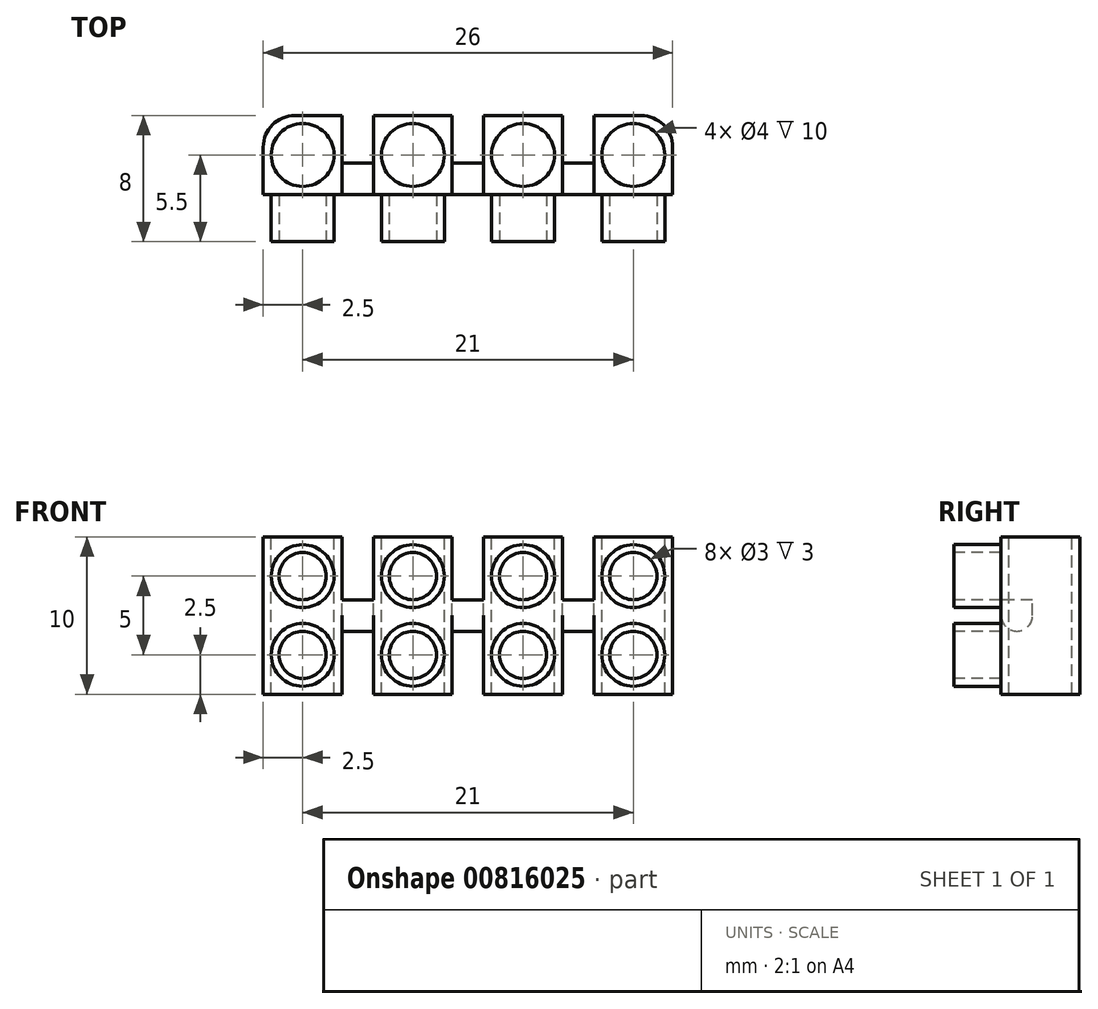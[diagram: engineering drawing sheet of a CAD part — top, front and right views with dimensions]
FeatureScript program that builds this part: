
annotation { "Feature Type Name" : "Feature", "Feature Type Description" : "" }
export const myFeature = defineFeature(function(context is Context, id is Id, definition is map)
    precondition{}
    {
        {
            var Q0;
            Q0=qCreatedBy(makeId("Front.planeOp"),FACE);
            var sketch = newSketch(context, id + "F0", { "sketchPlane" : qUnion([Q0])});
            skLineSegment(sketch, "E0.bottom", {"start": v(-13, 5) * mm, "end": v(13, 5) * mm});
            skLineSegment(sketch, "E0.top", {"start": v(-13, -5) * mm, "end": v(13, -5) * mm});
            skLineSegment(sketch, "E0.left", {"start": v(-13, 5) * mm, "end": v(-13, -5) * mm});
            skLineSegment(sketch, "E0.right", {"start": v(13, 5) * mm, "end": v(13, -5) * mm});
            skPoint(sketch, "E0.middle", {"position": v(0, 0) * mm});
            skSolve(sketch);
        }
        {
            var Q0;
            Q0=makeQuery(id+"F0.imprint","IMPRINT",FACE,{"disambiguationData":[TD([[makeQuery(id+"F0.imprint","IMPRINT",EDGE,{"derivedFrom":sQuery(id+"F0.wireOp",EDGE,"E0.bottom")}),-1.0]])]});
            extrude(context, id + "F1", {"entities" : qUnion([Q0]), "depth" : 8 * mm, "offsetDistance" : 25 * mm, "symmetric" : true});
        }
        {
            var Q0;
            Q0=makeQuery(id+"F1.opExtrude","CAP_FACE",FACE,{"disambiguationData":[OSD([sQuery(id+"F0.wireOp",EDGE,"E0.bottom"),sQuery(id+"F0.wireOp",EDGE,"E0.top"),sQuery(id+"F0.wireOp",EDGE,"E0.left"),sQuery(id+"F0.wireOp",EDGE,"E0.right")])],"isStart":false});
            var sketch = newSketch(context, id + "F2", { "sketchPlane" : qUnion([Q0])});
            skLineSegment(sketch, "E1", {"start": v(-13, 5) * mm, "end": v(-8, 5) * mm});
            skLineSegment(sketch, "E2", {"start": v(-8, 5) * mm, "end": v(-8, 1) * mm});
            skLineSegment(sketch, "E3", {"start": v(-8, 1) * mm, "end": v(-6, 1) * mm});
            skLineSegment(sketch, "E4", {"start": v(-6, 1) * mm, "end": v(-6, 5) * mm});
            skLineSegment(sketch, "E5", {"start": v(-6, 5) * mm, "end": v(-1, 5) * mm});
            skLineSegment(sketch, "E6", {"start": v(-1, 5) * mm, "end": v(-1, 1) * mm});
            skLineSegment(sketch, "E7", {"start": v(-1, 1) * mm, "end": v(1, 1) * mm});
            skLineSegment(sketch, "E8", {"start": v(1, 1) * mm, "end": v(1, 5) * mm});
            skLineSegment(sketch, "E9", {"start": v(1, 5) * mm, "end": v(6, 5) * mm});
            skLineSegment(sketch, "E10", {"start": v(6, 5) * mm, "end": v(6, 1) * mm});
            skLineSegment(sketch, "E11", {"start": v(6, 1) * mm, "end": v(8, 1) * mm});
            skLineSegment(sketch, "E12", {"start": v(8, 1) * mm, "end": v(8, 5) * mm});
            skLineSegment(sketch, "E13", {"start": v(8, 5) * mm, "end": v(13, 5) * mm});
            skLineSegment(sketch, "E14", {"start": v(13, 5) * mm, "end": v(13, -5) * mm});
            skLineSegment(sketch, "E15", {"start": v(13, -5) * mm, "end": v(8, -5) * mm});
            skLineSegment(sketch, "E16", {"start": v(8, -5) * mm, "end": v(8, -1) * mm});
            skLineSegment(sketch, "E17", {"start": v(8, -1) * mm, "end": v(6, -1) * mm});
            skLineSegment(sketch, "E18", {"start": v(6, -1) * mm, "end": v(6, -5) * mm});
            skLineSegment(sketch, "E19", {"start": v(6, -5) * mm, "end": v(1, -5) * mm});
            skLineSegment(sketch, "E20", {"start": v(1, -5) * mm, "end": v(1, -1) * mm});
            skLineSegment(sketch, "E21", {"start": v(1, -1) * mm, "end": v(-1, -1) * mm});
            skLineSegment(sketch, "E22", {"start": v(-1, -1) * mm, "end": v(-1, -5) * mm});
            skLineSegment(sketch, "E23", {"start": v(-1, -5) * mm, "end": v(-6, -5) * mm});
            skLineSegment(sketch, "E24", {"start": v(-6, -5) * mm, "end": v(-6, -1) * mm});
            skLineSegment(sketch, "E25", {"start": v(-6, -1) * mm, "end": v(-8, -1) * mm});
            skLineSegment(sketch, "E26", {"start": v(-8, -1) * mm, "end": v(-8, -5) * mm});
            skLineSegment(sketch, "E27", {"start": v(-8, -5) * mm, "end": v(-13, -5) * mm});
            skLineSegment(sketch, "E28", {"start": v(-13, -5) * mm, "end": v(-13, 5) * mm});
            skSolve(sketch);
        }
        {
            var Q0;
            {var subQ0=sQuery(id+"F2.wireOp",EDGE,"E2");Q0=makeQuery(id+"F2.imprint","IMPRINT",FACE,{"disambiguationData":[TD([[makeQuery(id+"F2.imprint","IMPRINT",EDGE,{"derivedFrom":subQ0}),1.0]])]});}
            var Q1;
            {var subQ0=sQuery(id+"F2.wireOp",EDGE,"E6");Q1=makeQuery(id+"F2.imprint","IMPRINT",FACE,{"disambiguationData":[TD([[makeQuery(id+"F2.imprint","IMPRINT",EDGE,{"derivedFrom":subQ0}),1.0]])]});}
            var Q2;
            {var subQ0=sQuery(id+"F2.wireOp",EDGE,"E10");Q2=makeQuery(id+"F2.imprint","IMPRINT",FACE,{"disambiguationData":[TD([[makeQuery(id+"F2.imprint","IMPRINT",EDGE,{"derivedFrom":subQ0}),1.0]])]});}
            var Q3;
            {var subQ0=sQuery(id+"F2.wireOp",EDGE,"E16");Q3=makeQuery(id+"F2.imprint","IMPRINT",FACE,{"disambiguationData":[TD([[makeQuery(id+"F2.imprint","IMPRINT",EDGE,{"derivedFrom":subQ0}),1.0]])]});}
            var Q4;
            {var subQ0=sQuery(id+"F2.wireOp",EDGE,"E20");Q4=makeQuery(id+"F2.imprint","IMPRINT",FACE,{"disambiguationData":[TD([[makeQuery(id+"F2.imprint","IMPRINT",EDGE,{"derivedFrom":subQ0}),1.0]])]});}
            var Q5;
            {var subQ0=sQuery(id+"F2.wireOp",EDGE,"E24");Q5=makeQuery(id+"F2.imprint","IMPRINT",FACE,{"disambiguationData":[TD([[makeQuery(id+"F2.imprint","IMPRINT",EDGE,{"derivedFrom":subQ0}),1.0]])]});}
            extrude(context, id + "F3", {"entities" : qUnion([Q0, Q1, Q2, Q3, Q4, Q5]), "operationType" : NewBodyOperationType.REMOVE, "oppositeDirection" : true, "depth" : 25 * mm, "offsetDistance" : 25 * mm});
        }
        {
            var Q0;
            Q0=makeQuery(id+"F3.boolean.opBoolean","COPY",FACE,{"derivedFrom":makeQuery(id+"F3.opExtrude","SWEPT_FACE",FACE,{"disambiguationData":[OSD([sQuery(id+"F2.wireOp",EDGE,"E7")])]})});
            var sketch = newSketch(context, id + "F4", { "sketchPlane" : qUnion([Q0])});
            skLineSegment(sketch, "E29.bottom", {"start": v(-1, -4) * mm, "end": v(1, -4) * mm});
            skLineSegment(sketch, "E29.top", {"start": v(-1, -1) * mm, "end": v(1, -1) * mm});
            skLineSegment(sketch, "E29.left", {"start": v(-1, -4) * mm, "end": v(-1, -1) * mm});
            skLineSegment(sketch, "E29.right", {"start": v(1, -4) * mm, "end": v(1, -1) * mm});
            skLineSegment(sketch, "E30.bottom", {"start": v(-1, 4) * mm, "end": v(1, 4) * mm});
            skLineSegment(sketch, "E30.top", {"start": v(-1, 1) * mm, "end": v(1, 1) * mm});
            skLineSegment(sketch, "E30.left", {"start": v(-1, 4) * mm, "end": v(-1, 1) * mm});
            skLineSegment(sketch, "E30.right", {"start": v(1, 4) * mm, "end": v(1, 1) * mm});
            skSolve(sketch);
        }
        {
            var Q0;
            Q0=makeQuery(id+"F3.boolean.opBoolean","COPY",FACE,{"derivedFrom":makeQuery(id+"F3.opExtrude","SWEPT_FACE",FACE,{"disambiguationData":[OSD([sQuery(id+"F2.wireOp",EDGE,"E11")])]})});
            var sketch = newSketch(context, id + "F5", { "sketchPlane" : qUnion([Q0])});
            skLineSegment(sketch, "E31.bottom", {"start": v(8, 4) * mm, "end": v(6, 4) * mm});
            skLineSegment(sketch, "E31.top", {"start": v(8, 1) * mm, "end": v(6, 1) * mm});
            skLineSegment(sketch, "E31.left", {"start": v(8, 4) * mm, "end": v(8, 1) * mm});
            skLineSegment(sketch, "E31.right", {"start": v(6, 4) * mm, "end": v(6, 1) * mm});
            skLineSegment(sketch, "E32.bottom", {"start": v(8, -4) * mm, "end": v(6, -4) * mm});
            skLineSegment(sketch, "E32.top", {"start": v(8, -1) * mm, "end": v(6, -1) * mm});
            skLineSegment(sketch, "E32.left", {"start": v(8, -4) * mm, "end": v(8, -1) * mm});
            skLineSegment(sketch, "E32.right", {"start": v(6, -4) * mm, "end": v(6, -1) * mm});
            skSolve(sketch);
        }
        {
            var Q0;
            Q0=makeQuery(id+"F3.boolean.opBoolean","COPY",FACE,{"derivedFrom":makeQuery(id+"F3.opExtrude","SWEPT_FACE",FACE,{"disambiguationData":[OSD([sQuery(id+"F2.wireOp",EDGE,"E3")])]})});
            var sketch = newSketch(context, id + "F6", { "sketchPlane" : qUnion([Q0])});
            skLineSegment(sketch, "E33.bottom", {"start": v(-6, -4) * mm, "end": v(-8, -4) * mm});
            skLineSegment(sketch, "E33.top", {"start": v(-6, -1) * mm, "end": v(-8, -1) * mm});
            skLineSegment(sketch, "E33.left", {"start": v(-6, -4) * mm, "end": v(-6, -1) * mm});
            skLineSegment(sketch, "E33.right", {"start": v(-8, -4) * mm, "end": v(-8, -1) * mm});
            skLineSegment(sketch, "E34.bottom", {"start": v(-6, 4) * mm, "end": v(-8, 4) * mm});
            skLineSegment(sketch, "E34.top", {"start": v(-6, 1) * mm, "end": v(-8, 1) * mm});
            skLineSegment(sketch, "E34.left", {"start": v(-6, 4) * mm, "end": v(-6, 1) * mm});
            skLineSegment(sketch, "E34.right", {"start": v(-8, 4) * mm, "end": v(-8, 1) * mm});
            skSolve(sketch);
        }
        {
            var Q0;
            Q0=makeQuery(id+"F4.imprint","IMPRINT",FACE,{"disambiguationData":[TD([[makeQuery(id+"F4.imprint","IMPRINT",EDGE,{"derivedFrom":sQuery(id+"F4.wireOp",EDGE,"E30.bottom")}),-1.0]])]});
            var Q1;
            Q1=makeQuery(id+"F4.imprint","IMPRINT",FACE,{"disambiguationData":[TD([[makeQuery(id+"F4.imprint","IMPRINT",EDGE,{"derivedFrom":sQuery(id+"F4.wireOp",EDGE,"E29.bottom")}),1.0]])]});
            var Q2;
            Q2=makeQuery(id+"F5.imprint","IMPRINT",FACE,{"disambiguationData":[TD([[makeQuery(id+"F5.imprint","IMPRINT",EDGE,{"derivedFrom":sQuery(id+"F5.wireOp",EDGE,"E31.bottom")}),-1.0]])]});
            var Q3;
            Q3=makeQuery(id+"F5.imprint","IMPRINT",FACE,{"disambiguationData":[TD([[makeQuery(id+"F5.imprint","IMPRINT",EDGE,{"derivedFrom":sQuery(id+"F5.wireOp",EDGE,"E32.bottom")}),1.0]])]});
            var Q4;
            Q4=makeQuery(id+"F6.imprint","IMPRINT",FACE,{"disambiguationData":[TD([[makeQuery(id+"F6.imprint","IMPRINT",EDGE,{"derivedFrom":sQuery(id+"F6.wireOp",EDGE,"E33.bottom")}),1.0]])]});
            var Q5;
            Q5=makeQuery(id+"F6.imprint","IMPRINT",FACE,{"disambiguationData":[TD([[makeQuery(id+"F6.imprint","IMPRINT",EDGE,{"derivedFrom":sQuery(id+"F6.wireOp",EDGE,"E34.bottom")}),-1.0]])]});
            extrude(context, id + "F7", {"entities" : qUnion([Q0, Q1, Q2, Q3, Q4, Q5]), "operationType" : NewBodyOperationType.REMOVE, "oppositeDirection" : true, "depth" : 25 * mm, "offsetDistance" : 25 * mm});
        }
        {
            var Q0;
            Q0=makeQuery(id+"F1.opExtrude","CAP_EDGE",EDGE,{"disambiguationData":[OSD([sQuery(id+"F0.wireOp",EDGE,"E0.left")])],"isStart":true});
            var Q1;
            {var subQ0=makeQuery(id+"F1.opExtrude","CAP_FACE",FACE,{"disambiguationData":[OSD([sQuery(id+"F0.wireOp",EDGE,"E0.bottom"),sQuery(id+"F0.wireOp",EDGE,"E0.top"),sQuery(id+"F0.wireOp",EDGE,"E0.left"),sQuery(id+"F0.wireOp",EDGE,"E0.right")])],"isStart":true});Q1=makeQuery(id+"F7.boolean.opBoolean","MERGE",EDGE,{"derivedFrom":[makeQuery(id+"F3.boolean.opBoolean","INTERSECT",EDGE,{"derivedFrom":[subQ0,makeQuery(id+"F3.opExtrude","SWEPT_FACE",FACE,{"disambiguationData":[OSD([sQuery(id+"F2.wireOp",EDGE,"E2")])]})]}),makeQuery(id+"F3.boolean.opBoolean","INTERSECT",EDGE,{"derivedFrom":[subQ0,makeQuery(id+"F3.opExtrude","SWEPT_FACE",FACE,{"disambiguationData":[OSD([sQuery(id+"F2.wireOp",EDGE,"E26")])]})]}),makeQuery(id+"F7.opExtrude","SWEPT_EDGE",EDGE,{"disambiguationData":[OSD([sQuery(id+"F6.wireOp",EDGE,"E34.bottom"),sQuery(id+"F6.wireOp",EDGE,"E34.right")])]})]});}
            var Q2;
            {var subQ0=makeQuery(id+"F1.opExtrude","CAP_FACE",FACE,{"disambiguationData":[OSD([sQuery(id+"F0.wireOp",EDGE,"E0.bottom"),sQuery(id+"F0.wireOp",EDGE,"E0.top"),sQuery(id+"F0.wireOp",EDGE,"E0.left"),sQuery(id+"F0.wireOp",EDGE,"E0.right")])],"isStart":true});Q2=makeQuery(id+"F7.boolean.opBoolean","MERGE",EDGE,{"derivedFrom":[makeQuery(id+"F3.boolean.opBoolean","INTERSECT",EDGE,{"derivedFrom":[subQ0,makeQuery(id+"F3.opExtrude","SWEPT_FACE",FACE,{"disambiguationData":[OSD([sQuery(id+"F2.wireOp",EDGE,"E4")])]})]}),makeQuery(id+"F3.boolean.opBoolean","INTERSECT",EDGE,{"derivedFrom":[subQ0,makeQuery(id+"F3.opExtrude","SWEPT_FACE",FACE,{"disambiguationData":[OSD([sQuery(id+"F2.wireOp",EDGE,"E24")])]})]}),makeQuery(id+"F7.opExtrude","SWEPT_EDGE",EDGE,{"disambiguationData":[OSD([sQuery(id+"F6.wireOp",EDGE,"E34.bottom"),sQuery(id+"F6.wireOp",EDGE,"E34.left")])]})]});}
            var Q3;
            {var subQ0=makeQuery(id+"F1.opExtrude","CAP_FACE",FACE,{"disambiguationData":[OSD([sQuery(id+"F0.wireOp",EDGE,"E0.bottom"),sQuery(id+"F0.wireOp",EDGE,"E0.top"),sQuery(id+"F0.wireOp",EDGE,"E0.left"),sQuery(id+"F0.wireOp",EDGE,"E0.right")])],"isStart":true});Q3=makeQuery(id+"F7.boolean.opBoolean","MERGE",EDGE,{"derivedFrom":[makeQuery(id+"F3.boolean.opBoolean","INTERSECT",EDGE,{"derivedFrom":[subQ0,makeQuery(id+"F3.opExtrude","SWEPT_FACE",FACE,{"disambiguationData":[OSD([sQuery(id+"F2.wireOp",EDGE,"E6")])]})]}),makeQuery(id+"F3.boolean.opBoolean","INTERSECT",EDGE,{"derivedFrom":[subQ0,makeQuery(id+"F3.opExtrude","SWEPT_FACE",FACE,{"disambiguationData":[OSD([sQuery(id+"F2.wireOp",EDGE,"E22")])]})]}),makeQuery(id+"F7.opExtrude","SWEPT_EDGE",EDGE,{"disambiguationData":[OSD([sQuery(id+"F4.wireOp",EDGE,"E30.bottom"),sQuery(id+"F4.wireOp",EDGE,"E30.left")])]})]});}
            var Q4;
            {var subQ0=makeQuery(id+"F1.opExtrude","CAP_FACE",FACE,{"disambiguationData":[OSD([sQuery(id+"F0.wireOp",EDGE,"E0.bottom"),sQuery(id+"F0.wireOp",EDGE,"E0.top"),sQuery(id+"F0.wireOp",EDGE,"E0.left"),sQuery(id+"F0.wireOp",EDGE,"E0.right")])],"isStart":true});Q4=makeQuery(id+"F7.boolean.opBoolean","MERGE",EDGE,{"derivedFrom":[makeQuery(id+"F3.boolean.opBoolean","INTERSECT",EDGE,{"derivedFrom":[subQ0,makeQuery(id+"F3.opExtrude","SWEPT_FACE",FACE,{"disambiguationData":[OSD([sQuery(id+"F2.wireOp",EDGE,"E8")])]})]}),makeQuery(id+"F3.boolean.opBoolean","INTERSECT",EDGE,{"derivedFrom":[subQ0,makeQuery(id+"F3.opExtrude","SWEPT_FACE",FACE,{"disambiguationData":[OSD([sQuery(id+"F2.wireOp",EDGE,"E20")])]})]}),makeQuery(id+"F7.opExtrude","SWEPT_EDGE",EDGE,{"disambiguationData":[OSD([sQuery(id+"F4.wireOp",EDGE,"E30.bottom"),sQuery(id+"F4.wireOp",EDGE,"E30.right")])]})]});}
            var Q5;
            {var subQ0=makeQuery(id+"F1.opExtrude","CAP_FACE",FACE,{"disambiguationData":[OSD([sQuery(id+"F0.wireOp",EDGE,"E0.bottom"),sQuery(id+"F0.wireOp",EDGE,"E0.top"),sQuery(id+"F0.wireOp",EDGE,"E0.left"),sQuery(id+"F0.wireOp",EDGE,"E0.right")])],"isStart":true});Q5=makeQuery(id+"F7.boolean.opBoolean","MERGE",EDGE,{"derivedFrom":[makeQuery(id+"F3.boolean.opBoolean","INTERSECT",EDGE,{"derivedFrom":[subQ0,makeQuery(id+"F3.opExtrude","SWEPT_FACE",FACE,{"disambiguationData":[OSD([sQuery(id+"F2.wireOp",EDGE,"E10")])]})]}),makeQuery(id+"F3.boolean.opBoolean","INTERSECT",EDGE,{"derivedFrom":[subQ0,makeQuery(id+"F3.opExtrude","SWEPT_FACE",FACE,{"disambiguationData":[OSD([sQuery(id+"F2.wireOp",EDGE,"E18")])]})]}),makeQuery(id+"F7.opExtrude","SWEPT_EDGE",EDGE,{"disambiguationData":[OSD([sQuery(id+"F5.wireOp",EDGE,"E31.bottom"),sQuery(id+"F5.wireOp",EDGE,"E31.right")])]})]});}
            var Q6;
            {var subQ0=makeQuery(id+"F1.opExtrude","CAP_FACE",FACE,{"disambiguationData":[OSD([sQuery(id+"F0.wireOp",EDGE,"E0.bottom"),sQuery(id+"F0.wireOp",EDGE,"E0.top"),sQuery(id+"F0.wireOp",EDGE,"E0.left"),sQuery(id+"F0.wireOp",EDGE,"E0.right")])],"isStart":true});Q6=makeQuery(id+"F7.boolean.opBoolean","MERGE",EDGE,{"derivedFrom":[makeQuery(id+"F3.boolean.opBoolean","INTERSECT",EDGE,{"derivedFrom":[subQ0,makeQuery(id+"F3.opExtrude","SWEPT_FACE",FACE,{"disambiguationData":[OSD([sQuery(id+"F2.wireOp",EDGE,"E12")])]})]}),makeQuery(id+"F3.boolean.opBoolean","INTERSECT",EDGE,{"derivedFrom":[subQ0,makeQuery(id+"F3.opExtrude","SWEPT_FACE",FACE,{"disambiguationData":[OSD([sQuery(id+"F2.wireOp",EDGE,"E16")])]})]}),makeQuery(id+"F7.opExtrude","SWEPT_EDGE",EDGE,{"disambiguationData":[OSD([sQuery(id+"F5.wireOp",EDGE,"E31.bottom"),sQuery(id+"F5.wireOp",EDGE,"E31.left")])]})]});}
            var Q7;
            Q7=makeQuery(id+"F1.opExtrude","CAP_EDGE",EDGE,{"disambiguationData":[OSD([sQuery(id+"F0.wireOp",EDGE,"E0.right")])],"isStart":true});
            fillet(context, id + "F8", {"entities" : qUnion([Q0, Q1, Q2, Q3, Q4, Q5, Q6, Q7]), "radius" : 2 * mm, "tangentPropagation" : true, "allowEdgeOverflow" : false});
        }
        {
            var Q0;
            {var subQ1=sQuery(id+"F0.wireOp",EDGE,"E0.left");var subQ3=sQuery(id+"F0.wireOp",EDGE,"E0.bottom");Q0=makeQuery(id+"F3.boolean.opBoolean","SPLIT",FACE,{"disambiguationData":[TD([makeQuery(id+"F1.opExtrude","SWEPT_FACE",FACE,{"disambiguationData":[OSD([subQ1])]})])],"derivedFrom":makeQuery(id+"F1.opExtrude","SWEPT_FACE",FACE,{"disambiguationData":[OSD([subQ3])]})});}
            var sketch = newSketch(context, id + "F9", { "sketchPlane" : qUnion([Q0])});
            skLineSegment(sketch, "E35", {"start": v(-10.5, 4) * mm, "end": v(-10.5, 1.5) * mm});
            skCircle(sketch, "E36", {"center": v(-10.5, 1.5) * mm, "radius": 2 * mm});
            skSolve(sketch);
        }
        {
            var Q0;
            {var subQ3=sQuery(id+"F0.wireOp",EDGE,"E0.bottom");Q0=makeQuery(id+"F3.boolean.opBoolean","SPLIT",FACE,{"disambiguationData":[TD([makeQuery(id+"F3.opExtrude","SWEPT_FACE",FACE,{"disambiguationData":[OSD([sQuery(id+"F2.wireOp",EDGE,"E4")])]})])],"derivedFrom":makeQuery(id+"F1.opExtrude","SWEPT_FACE",FACE,{"disambiguationData":[OSD([subQ3])]})});}
            var sketch = newSketch(context, id + "F10", { "sketchPlane" : qUnion([Q0])});
            skLineSegment(sketch, "E37", {"start": v(-3.5, 4) * mm, "end": v(-3.5, 1.5) * mm});
            skCircle(sketch, "E38", {"center": v(-3.5, 1.5) * mm, "radius": 2 * mm});
            skSolve(sketch);
        }
        {
            var Q0;
            {var subQ3=sQuery(id+"F0.wireOp",EDGE,"E0.bottom");Q0=makeQuery(id+"F3.boolean.opBoolean","SPLIT",FACE,{"disambiguationData":[TD([makeQuery(id+"F3.opExtrude","SWEPT_FACE",FACE,{"disambiguationData":[OSD([sQuery(id+"F2.wireOp",EDGE,"E8")])]})])],"derivedFrom":makeQuery(id+"F1.opExtrude","SWEPT_FACE",FACE,{"disambiguationData":[OSD([subQ3])]})});}
            var sketch = newSketch(context, id + "F11", { "sketchPlane" : qUnion([Q0])});
            skLineSegment(sketch, "E39", {"start": v(3.5, 4) * mm, "end": v(3.5, 1.5) * mm});
            skCircle(sketch, "E40", {"center": v(3.5, 1.5) * mm, "radius": 2 * mm});
            skSolve(sketch);
        }
        {
            var Q0;
            {var subQ0=sQuery(id+"F0.wireOp",EDGE,"E0.right");var subQ3=sQuery(id+"F0.wireOp",EDGE,"E0.bottom");Q0=makeQuery(id+"F3.boolean.opBoolean","SPLIT",FACE,{"disambiguationData":[TD([makeQuery(id+"F1.opExtrude","SWEPT_FACE",FACE,{"disambiguationData":[OSD([subQ0])]})])],"derivedFrom":makeQuery(id+"F1.opExtrude","SWEPT_FACE",FACE,{"disambiguationData":[OSD([subQ3])]})});}
            var sketch = newSketch(context, id + "F12", { "sketchPlane" : qUnion([Q0])});
            skLineSegment(sketch, "E41", {"start": v(10.5, 4) * mm, "end": v(10.5, 1.5) * mm});
            skCircle(sketch, "E42", {"center": v(10.5, 1.5) * mm, "radius": 2 * mm});
            skSolve(sketch);
        }
        {
            var Q0;
            Q0=makeQuery(id+"F10.imprint","IMPRINT",FACE,{"disambiguationData":[TD([[makeQuery(id+"F10.imprint","IMPRINT",EDGE,{"derivedFrom":sQuery(id+"F10.wireOp",EDGE,"E38")}),1.0]])]});
            var Q1;
            Q1=makeQuery(id+"F11.imprint","IMPRINT",FACE,{"disambiguationData":[TD([[makeQuery(id+"F11.imprint","IMPRINT",EDGE,{"derivedFrom":sQuery(id+"F11.wireOp",EDGE,"E40")}),1.0]])]});
            var Q2;
            Q2=makeQuery(id+"F12.imprint","IMPRINT",FACE,{"disambiguationData":[TD([[makeQuery(id+"F12.imprint","IMPRINT",EDGE,{"derivedFrom":sQuery(id+"F12.wireOp",EDGE,"E42")}),1.0]])]});
            var Q3;
            {var subQ2=sQuery(id+"F0.wireOp",EDGE,"E0.top");Q3=makeQuery(id+"F3.boolean.opBoolean","SPLIT",FACE,{"disambiguationData":[TD([makeQuery(id+"F3.opExtrude","SWEPT_FACE",FACE,{"disambiguationData":[OSD([sQuery(id+"F2.wireOp",EDGE,"E22")])]})])],"derivedFrom":makeQuery(id+"F1.opExtrude","SWEPT_FACE",FACE,{"disambiguationData":[OSD([subQ2])]})});}
            var Q4;
            Q4=makeQuery(id+"F9.imprint","IMPRINT",FACE,{"disambiguationData":[TD([[makeQuery(id+"F9.imprint","IMPRINT",EDGE,{"derivedFrom":sQuery(id+"F9.wireOp",EDGE,"E36")}),1.0]])]});
            extrude(context, id + "F13", {"entities" : qUnion([Q0, Q1, Q2, Q3, Q4]), "operationType" : NewBodyOperationType.REMOVE, "oppositeDirection" : true, "depth" : 25 * mm, "offsetDistance" : 25 * mm});
        }
        {
            var Q0;
            Q0=makeQuery(id+"F7.boolean.opBoolean","COPY",EDGE,{"derivedFrom":makeQuery(id+"F7.opExtrude","CAP_EDGE",EDGE,{"disambiguationData":[OSD([sQuery(id+"F6.wireOp",EDGE,"E33.top")])],"isStart":true})});
            var Q1;
            Q1=makeQuery(id+"F7.boolean.opBoolean","INTERSECT",EDGE,{"derivedFrom":[makeQuery(id+"F3.boolean.opBoolean","COPY",FACE,{"derivedFrom":makeQuery(id+"F3.opExtrude","SWEPT_FACE",FACE,{"disambiguationData":[OSD([sQuery(id+"F2.wireOp",EDGE,"E25")])]})}),makeQuery(id+"F7.opExtrude","SWEPT_FACE",FACE,{"disambiguationData":[OSD([sQuery(id+"F6.wireOp",EDGE,"E33.top")])]})]});
            var Q2;
            Q2=makeQuery(id+"F7.boolean.opBoolean","COPY",EDGE,{"derivedFrom":makeQuery(id+"F7.opExtrude","CAP_EDGE",EDGE,{"disambiguationData":[OSD([sQuery(id+"F4.wireOp",EDGE,"E29.top")])],"isStart":true})});
            var Q3;
            Q3=makeQuery(id+"F7.boolean.opBoolean","INTERSECT",EDGE,{"derivedFrom":[makeQuery(id+"F3.boolean.opBoolean","COPY",FACE,{"derivedFrom":makeQuery(id+"F3.opExtrude","SWEPT_FACE",FACE,{"disambiguationData":[OSD([sQuery(id+"F2.wireOp",EDGE,"E21")])]})}),makeQuery(id+"F7.opExtrude","SWEPT_FACE",FACE,{"disambiguationData":[OSD([sQuery(id+"F4.wireOp",EDGE,"E29.top")])]})]});
            var Q4;
            Q4=makeQuery(id+"F7.boolean.opBoolean","COPY",EDGE,{"derivedFrom":makeQuery(id+"F7.opExtrude","CAP_EDGE",EDGE,{"disambiguationData":[OSD([sQuery(id+"F5.wireOp",EDGE,"E32.top")])],"isStart":true})});
            var Q5;
            Q5=makeQuery(id+"F7.boolean.opBoolean","INTERSECT",EDGE,{"derivedFrom":[makeQuery(id+"F3.boolean.opBoolean","COPY",FACE,{"derivedFrom":makeQuery(id+"F3.opExtrude","SWEPT_FACE",FACE,{"disambiguationData":[OSD([sQuery(id+"F2.wireOp",EDGE,"E17")])]})}),makeQuery(id+"F7.opExtrude","SWEPT_FACE",FACE,{"disambiguationData":[OSD([sQuery(id+"F5.wireOp",EDGE,"E32.top")])]})]});
            var Q6;
            Q6=makeQuery(id+"F7.boolean.opBoolean","COPY",EDGE,{"derivedFrom":makeQuery(id+"F7.opExtrude","CAP_EDGE",EDGE,{"disambiguationData":[OSD([sQuery(id+"F4.wireOp",EDGE,"E30.top")])],"isStart":true})});
            var Q7;
            Q7=makeQuery(id+"F7.boolean.opBoolean","INTERSECT",EDGE,{"derivedFrom":[makeQuery(id+"F3.boolean.opBoolean","COPY",FACE,{"derivedFrom":makeQuery(id+"F3.opExtrude","SWEPT_FACE",FACE,{"disambiguationData":[OSD([sQuery(id+"F2.wireOp",EDGE,"E21")])]})}),makeQuery(id+"F7.opExtrude","SWEPT_FACE",FACE,{"disambiguationData":[OSD([sQuery(id+"F4.wireOp",EDGE,"E30.top")])]})]});
            var Q8;
            Q8=makeQuery(id+"F7.boolean.opBoolean","INTERSECT",EDGE,{"derivedFrom":[makeQuery(id+"F3.boolean.opBoolean","COPY",FACE,{"derivedFrom":makeQuery(id+"F3.opExtrude","SWEPT_FACE",FACE,{"disambiguationData":[OSD([sQuery(id+"F2.wireOp",EDGE,"E25")])]})}),makeQuery(id+"F7.opExtrude","SWEPT_FACE",FACE,{"disambiguationData":[OSD([sQuery(id+"F6.wireOp",EDGE,"E34.top")])]})]});
            var Q9;
            Q9=makeQuery(id+"F7.boolean.opBoolean","COPY",EDGE,{"derivedFrom":makeQuery(id+"F7.opExtrude","CAP_EDGE",EDGE,{"disambiguationData":[OSD([sQuery(id+"F6.wireOp",EDGE,"E34.top")])],"isStart":true})});
            var Q10;
            Q10=makeQuery(id+"F7.boolean.opBoolean","INTERSECT",EDGE,{"derivedFrom":[makeQuery(id+"F3.boolean.opBoolean","COPY",FACE,{"derivedFrom":makeQuery(id+"F3.opExtrude","SWEPT_FACE",FACE,{"disambiguationData":[OSD([sQuery(id+"F2.wireOp",EDGE,"E17")])]})}),makeQuery(id+"F7.opExtrude","SWEPT_FACE",FACE,{"disambiguationData":[OSD([sQuery(id+"F5.wireOp",EDGE,"E31.top")])]})]});
            var Q11;
            Q11=makeQuery(id+"F7.boolean.opBoolean","COPY",EDGE,{"derivedFrom":makeQuery(id+"F7.opExtrude","CAP_EDGE",EDGE,{"disambiguationData":[OSD([sQuery(id+"F5.wireOp",EDGE,"E31.top")])],"isStart":true})});
            fillet(context, id + "F14", {"entities" : qUnion([Q0, Q1, Q2, Q3, Q4, Q5, Q6, Q7, Q8, Q9, Q10, Q11]), "radius" : 1 * mm, "tangentPropagation" : true, "allowEdgeOverflow" : false});
        }
        {
            var Q0;
            {var subQ0=sQuery(id+"F0.wireOp",EDGE,"E0.left");var subQ1=sQuery(id+"F0.wireOp",EDGE,"E0.top");var subQ2=sQuery(id+"F0.wireOp",EDGE,"E0.bottom");Q0=makeQuery(id+"F7.boolean.opBoolean","SPLIT",FACE,{"disambiguationData":[TD([makeQuery(id+"F1.opExtrude","SWEPT_FACE",FACE,{"disambiguationData":[OSD([subQ0])]})])],"derivedFrom":makeQuery(id+"F1.opExtrude","CAP_FACE",FACE,{"disambiguationData":[OSD([subQ2,subQ1,subQ0,sQuery(id+"F0.wireOp",EDGE,"E0.right")])],"isStart":false})});}
            var sketch = newSketch(context, id + "F15", { "sketchPlane" : qUnion([Q0])});
            skLineSegment(sketch, "E43", {"start": v(-10.5, 5) * mm, "end": v(-10.5, 2.5) * mm});
            skLineSegment(sketch, "E44", {"start": v(-10.5, 2.5) * mm, "end": v(-10.5, -2.5) * mm});
            skCircle(sketch, "E45", {"center": v(-10.5, 2.5) * mm, "radius": 1.5 * mm});
            skCircle(sketch, "E46", {"center": v(-10.5, -2.5) * mm, "radius": 1.5 * mm});
            skCircle(sketch, "E47.0", {"center": v(-10.5, 2.5) * mm, "radius": 2 * mm});
            skCircle(sketch, "E48.0", {"center": v(-10.5, -2.5) * mm, "radius": 2 * mm});
            skSolve(sketch);
        }
        {
            var Q0;
            {var subQ0=sQuery(id+"F0.wireOp",EDGE,"E0.top");var subQ1=sQuery(id+"F0.wireOp",EDGE,"E0.bottom");Q0=makeQuery(id+"F7.boolean.opBoolean","SPLIT",FACE,{"disambiguationData":[TD([makeQuery(id+"F3.boolean.opBoolean","COPY",FACE,{"derivedFrom":makeQuery(id+"F3.opExtrude","SWEPT_FACE",FACE,{"disambiguationData":[OSD([sQuery(id+"F2.wireOp",EDGE,"E4")])]})})])],"derivedFrom":makeQuery(id+"F1.opExtrude","CAP_FACE",FACE,{"disambiguationData":[OSD([subQ1,subQ0,sQuery(id+"F0.wireOp",EDGE,"E0.left"),sQuery(id+"F0.wireOp",EDGE,"E0.right")])],"isStart":false})});}
            var sketch = newSketch(context, id + "F16", { "sketchPlane" : qUnion([Q0])});
            skLineSegment(sketch, "E49", {"start": v(-3.5, 5) * mm, "end": v(-3.5, 2.5) * mm});
            skLineSegment(sketch, "E50", {"start": v(-3.5, 2.5) * mm, "end": v(-3.5, -2.5) * mm});
            skCircle(sketch, "E51", {"center": v(-3.5, 2.5) * mm, "radius": 1.5 * mm});
            skCircle(sketch, "E52", {"center": v(-3.5, -2.5) * mm, "radius": 1.5 * mm});
            skCircle(sketch, "E53.0", {"center": v(-3.5, 2.5) * mm, "radius": 2 * mm});
            skCircle(sketch, "E54.0", {"center": v(-3.5, -2.5) * mm, "radius": 2 * mm});
            skSolve(sketch);
        }
        {
            var Q0;
            {var subQ0=sQuery(id+"F0.wireOp",EDGE,"E0.top");var subQ1=sQuery(id+"F0.wireOp",EDGE,"E0.bottom");Q0=makeQuery(id+"F7.boolean.opBoolean","SPLIT",FACE,{"disambiguationData":[TD([makeQuery(id+"F3.boolean.opBoolean","COPY",FACE,{"derivedFrom":makeQuery(id+"F3.opExtrude","SWEPT_FACE",FACE,{"disambiguationData":[OSD([sQuery(id+"F2.wireOp",EDGE,"E8")])]})})])],"derivedFrom":makeQuery(id+"F1.opExtrude","CAP_FACE",FACE,{"disambiguationData":[OSD([subQ1,subQ0,sQuery(id+"F0.wireOp",EDGE,"E0.left"),sQuery(id+"F0.wireOp",EDGE,"E0.right")])],"isStart":false})});}
            var sketch = newSketch(context, id + "F17", { "sketchPlane" : qUnion([Q0])});
            skLineSegment(sketch, "E55", {"start": v(3.5, 5) * mm, "end": v(3.5, 2.5) * mm});
            skLineSegment(sketch, "E56", {"start": v(3.5, 2.5) * mm, "end": v(3.5, -2.5) * mm});
            skCircle(sketch, "E57", {"center": v(3.5, 2.5) * mm, "radius": 1.5 * mm});
            skCircle(sketch, "E58", {"center": v(3.5, -2.5) * mm, "radius": 1.5 * mm});
            skCircle(sketch, "E59.0", {"center": v(3.5, 2.5) * mm, "radius": 2 * mm});
            skCircle(sketch, "E60.0", {"center": v(3.5, -2.5) * mm, "radius": 2 * mm});
            skSolve(sketch);
        }
        {
            var Q0;
            {var subQ0=sQuery(id+"F0.wireOp",EDGE,"E0.top");var subQ1=sQuery(id+"F0.wireOp",EDGE,"E0.right");var subQ2=sQuery(id+"F0.wireOp",EDGE,"E0.bottom");Q0=makeQuery(id+"F7.boolean.opBoolean","SPLIT",FACE,{"disambiguationData":[TD([makeQuery(id+"F1.opExtrude","SWEPT_FACE",FACE,{"disambiguationData":[OSD([subQ1])]})])],"derivedFrom":makeQuery(id+"F1.opExtrude","CAP_FACE",FACE,{"disambiguationData":[OSD([subQ2,subQ0,sQuery(id+"F0.wireOp",EDGE,"E0.left"),subQ1])],"isStart":false})});}
            var sketch = newSketch(context, id + "F18", { "sketchPlane" : qUnion([Q0])});
            skLineSegment(sketch, "E61", {"start": v(10.5, 5) * mm, "end": v(10.5, 2.5) * mm});
            skLineSegment(sketch, "E62", {"start": v(10.5, 2.5) * mm, "end": v(10.5, -2.5) * mm});
            skCircle(sketch, "E63", {"center": v(10.5, 2.5) * mm, "radius": 1.5 * mm});
            skCircle(sketch, "E64", {"center": v(10.5, -2.5) * mm, "radius": 1.5 * mm});
            skCircle(sketch, "E65.0", {"center": v(10.5, 2.5) * mm, "radius": 2 * mm});
            skCircle(sketch, "E66.0", {"center": v(10.5, -2.5) * mm, "radius": 2 * mm});
            skSolve(sketch);
        }
        {
            var Q0;
            Q0=makeQuery(id+"F18.imprint","IMPRINT",FACE,{"disambiguationData":[TD([[makeQuery(id+"F18.imprint","IMPRINT",EDGE,{"derivedFrom":sQuery(id+"F18.wireOp",EDGE,"E66.0")}),-1.0]])]});
            var Q1;
            Q1=makeQuery(id+"F17.imprint","IMPRINT",FACE,{"disambiguationData":[TD([[makeQuery(id+"F17.imprint","IMPRINT",EDGE,{"derivedFrom":sQuery(id+"F17.wireOp",EDGE,"E60.0")}),-1.0]])]});
            var Q2;
            Q2=makeQuery(id+"F16.imprint","IMPRINT",FACE,{"disambiguationData":[TD([[makeQuery(id+"F16.imprint","IMPRINT",EDGE,{"derivedFrom":sQuery(id+"F16.wireOp",EDGE,"E54.0")}),-1.0]])]});
            var Q3;
            Q3=makeQuery(id+"F15.imprint","IMPRINT",FACE,{"disambiguationData":[TD([[makeQuery(id+"F15.imprint","IMPRINT",EDGE,{"derivedFrom":sQuery(id+"F15.wireOp",EDGE,"E48.0")}),-1.0]])]});
            var Q4;
            {var subQ0=sQuery(id+"F18.wireOp",EDGE,"E62");var subQ1=sQuery(id+"F18.wireOp",EDGE,"E61");var subQ2=makeQuery(id+"F18.imprint","INTERSECT",VERTEX,{"derivedFrom":[subQ1,subQ0]});Q4=makeQuery(id+"F18.imprint","IMPRINT",FACE,{"disambiguationData":[TD([[makeQuery(id+"F18.imprint","IMPRINT",EDGE,{"disambiguationData":[TD([[subQ2,1.0]])],"derivedFrom":subQ1}),1.0]])]});}
            var Q5;
            {var subQ0=sQuery(id+"F18.wireOp",EDGE,"E62");var subQ1=sQuery(id+"F18.wireOp",EDGE,"E61");var subQ2=makeQuery(id+"F18.imprint","INTERSECT",VERTEX,{"derivedFrom":[subQ1,subQ0]});Q5=makeQuery(id+"F18.imprint","IMPRINT",FACE,{"disambiguationData":[TD([[makeQuery(id+"F18.imprint","IMPRINT",EDGE,{"disambiguationData":[TD([[subQ2,1.0]])],"derivedFrom":subQ1}),-1.0]])]});}
            var Q6;
            Q6=makeQuery(id+"F18.imprint","IMPRINT",FACE,{"disambiguationData":[TD([[makeQuery(id+"F18.imprint","IMPRINT",EDGE,{"derivedFrom":sQuery(id+"F18.wireOp",EDGE,"E64")}),1.0]])]});
            var Q7;
            Q7=makeQuery(id+"F17.imprint","IMPRINT",FACE,{"disambiguationData":[TD([[makeQuery(id+"F17.imprint","IMPRINT",EDGE,{"derivedFrom":sQuery(id+"F17.wireOp",EDGE,"E58")}),1.0]])]});
            var Q8;
            Q8=makeQuery(id+"F16.imprint","IMPRINT",FACE,{"disambiguationData":[TD([[makeQuery(id+"F16.imprint","IMPRINT",EDGE,{"derivedFrom":sQuery(id+"F16.wireOp",EDGE,"E52")}),1.0]])]});
            var Q9;
            Q9=makeQuery(id+"F15.imprint","IMPRINT",FACE,{"disambiguationData":[TD([[makeQuery(id+"F15.imprint","IMPRINT",EDGE,{"derivedFrom":sQuery(id+"F15.wireOp",EDGE,"E46")}),1.0]])]});
            var Q10;
            {var subQ0=sQuery(id+"F15.wireOp",EDGE,"E44");var subQ1=sQuery(id+"F15.wireOp",EDGE,"E43");var subQ2=makeQuery(id+"F15.imprint","INTERSECT",VERTEX,{"derivedFrom":[subQ1,subQ0]});Q10=makeQuery(id+"F15.imprint","IMPRINT",FACE,{"disambiguationData":[TD([[makeQuery(id+"F15.imprint","IMPRINT",EDGE,{"disambiguationData":[TD([[subQ2,1.0]])],"derivedFrom":subQ1}),-1.0]])]});}
            var Q11;
            {var subQ0=sQuery(id+"F15.wireOp",EDGE,"E44");var subQ1=sQuery(id+"F15.wireOp",EDGE,"E43");var subQ2=makeQuery(id+"F15.imprint","INTERSECT",VERTEX,{"derivedFrom":[subQ1,subQ0]});Q11=makeQuery(id+"F15.imprint","IMPRINT",FACE,{"disambiguationData":[TD([[makeQuery(id+"F15.imprint","IMPRINT",EDGE,{"disambiguationData":[TD([[subQ2,1.0]])],"derivedFrom":subQ1}),1.0]])]});}
            var Q12;
            {var subQ0=sQuery(id+"F16.wireOp",EDGE,"E50");var subQ1=sQuery(id+"F16.wireOp",EDGE,"E49");var subQ2=makeQuery(id+"F16.imprint","INTERSECT",VERTEX,{"derivedFrom":[subQ1,subQ0]});Q12=makeQuery(id+"F16.imprint","IMPRINT",FACE,{"disambiguationData":[TD([[makeQuery(id+"F16.imprint","IMPRINT",EDGE,{"disambiguationData":[TD([[subQ2,1.0]])],"derivedFrom":subQ1}),-1.0]])]});}
            var Q13;
            {var subQ0=sQuery(id+"F16.wireOp",EDGE,"E50");var subQ1=sQuery(id+"F16.wireOp",EDGE,"E49");var subQ2=makeQuery(id+"F16.imprint","INTERSECT",VERTEX,{"derivedFrom":[subQ1,subQ0]});Q13=makeQuery(id+"F16.imprint","IMPRINT",FACE,{"disambiguationData":[TD([[makeQuery(id+"F16.imprint","IMPRINT",EDGE,{"disambiguationData":[TD([[subQ2,1.0]])],"derivedFrom":subQ1}),1.0]])]});}
            var Q14;
            {var subQ0=sQuery(id+"F17.wireOp",EDGE,"E56");var subQ1=sQuery(id+"F17.wireOp",EDGE,"E55");var subQ2=makeQuery(id+"F17.imprint","INTERSECT",VERTEX,{"derivedFrom":[subQ1,subQ0]});Q14=makeQuery(id+"F17.imprint","IMPRINT",FACE,{"disambiguationData":[TD([[makeQuery(id+"F17.imprint","IMPRINT",EDGE,{"disambiguationData":[TD([[subQ2,1.0]])],"derivedFrom":subQ1}),-1.0]])]});}
            var Q15;
            {var subQ0=sQuery(id+"F17.wireOp",EDGE,"E56");var subQ1=sQuery(id+"F17.wireOp",EDGE,"E55");var subQ2=makeQuery(id+"F17.imprint","INTERSECT",VERTEX,{"derivedFrom":[subQ1,subQ0]});Q15=makeQuery(id+"F17.imprint","IMPRINT",FACE,{"disambiguationData":[TD([[makeQuery(id+"F17.imprint","IMPRINT",EDGE,{"disambiguationData":[TD([[subQ2,1.0]])],"derivedFrom":subQ1}),1.0]])]});}
            extrude(context, id + "F19", {"entities" : qUnion([Q0, Q1, Q2, Q3, Q4, Q5, Q6, Q7, Q8, Q9, Q10, Q11, Q12, Q13, Q14, Q15]), "operationType" : NewBodyOperationType.REMOVE, "oppositeDirection" : true, "depth" : 3 * mm, "offsetDistance" : 25 * mm});
        }
    });
